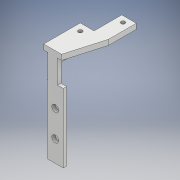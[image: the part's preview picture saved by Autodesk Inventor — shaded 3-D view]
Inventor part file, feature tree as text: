
AUTODESK INVENTOR PART (.ipt)
format: ipt  version: 2018.3 (Build 223284000, 284)  size: 1,041,408 bytes
history: native  units: mm
features: extrude x95, sketch x95, other x2
ambient origin geometry x8: Origin, YZ Plane, XZ Plane, XY Plane, X Axis, Y Axis, Z Axis, Center Point
bodies: Body1 (feature_tree), Body2 (feature_tree)
feature tree (192):
  other  "Sólido1"
  extrude  "Extrusión1"  Depth=10.0mm TaperAngle=0.0deg
  extrude  "Extrusión2"  Depth=33.0mm TaperAngle=0.0deg
  extrude  "Extrusión3"  Depth=29.0mm TaperAngle=0.0deg
  extrude  "Extrusión4"  Depth=21.0mm
  extrude  "Extrusión5"  Depth=4.0mm TaperAngle=0.0deg
  extrude  "Extrusión6"  Depth=37.0mm TaperAngle=0.0deg
  extrude  "Extrusión7"  Depth=94.0mm TaperAngle=0.0deg
  extrude  "Extrusión8"  Depth=15.0mm
  extrude  "Extrusión9"  Depth=64.0mm TaperAngle=0.0deg
  extrude  "Extrusión10"  Depth=10.0mm
  extrude  "Extrusión11"  Depth=64.0mm TaperAngle=0.0deg
  extrude  "Extrusión13"  Depth=10.0mm
  extrude  "Extrusión14"  Depth=10.0mm
  extrude  "Extrusión15"  Depth=19.0mm TaperAngle=0.0deg
  extrude  "Extrusión17"  Depth=19.0mm TaperAngle=0.0deg
  extrude  "Extrusión18"  Depth=15.0mm TaperAngle=0.0deg
  extrude  "Extrusión19"  Depth=3.0mm
  extrude  "Extrusión20"  Depth=6.0mm TaperAngle=0.0deg
  extrude  "Extrusión21"  Depth=10.0mm TaperAngle=0.0deg
  extrude  "Extrusión22"  Depth=10.0mm TaperAngle=0.0deg
  extrude  "Extrusión23"  Depth=10.0mm TaperAngle=0.0deg
  extrude  "Extrusión27"  Depth=15.0mm
  extrude  "Extrusión28"  Depth=5.0mm
  extrude  "Extrusión29"  Depth=4.0mm TaperAngle=0.0deg
  extrude  "Extrusión30"  Depth=24.5mm TaperAngle=0.0deg
  extrude  "Extrusión31"  Depth=24.5mm TaperAngle=0.0deg
  extrude  "Extrusión32"  Depth=4.3mm
  extrude  "Extrusión33"  Depth=3.7mm
  sketch  "Boceto34"  dims[d152=3.7mm d153=3.7mm]
  extrude  "Extrusión35"  Depth=3.7mm
  extrude  "Extrusión36"  Depth=25.5mm TaperAngle=0.0deg
  extrude  "Extrusión38"  Depth=5.2mm
  extrude  "Extrusión39"  Depth=5.2mm
  extrude  "Extrusión40"  Depth=45.25mm TaperAngle=0.0deg
  extrude  "Extrusión41"  Depth=71.0mm TaperAngle=0.0deg
  extrude  "Extrusión42"  Depth=1.7mm TaperAngle=0.0deg
  extrude  "Extrusión43"  Depth=33.0mm
  extrude  "Extrusión44"  Depth=2.4mm TaperAngle=0.0deg
  extrude  "Extrusión45"  Depth=85.9mm TaperAngle=0.0deg
  extrude  "Extrusión46"  Depth=2.973mm
  extrude  "Extrusión47"  Depth=3.7mm
  extrude  "Extrusión48"  Depth=3.7mm
  extrude  "Extrusión49"  Depth=5.0mm TaperAngle=0.0deg
  extrude  "Extrusión50"  Depth=0.534mm
  extrude  "Extrusión53"  Depth=2.384mm TaperAngle=0.0deg
  extrude  "Extrusión54"  Depth=5.884mm TaperAngle=0.0deg
  extrude  "Extrusión55"  Depth=14.25mm TaperAngle=0.0deg
  extrude  "Extrusión56"  Depth=11.0mm TaperAngle=0.0deg
  extrude  "Extrusión57"  Depth=3.1mm
  sketch  "Boceto57"  dims[d235=11.0mm d236=0.0mm d237=11.0mm]
  extrude  "Extrusión58"  Depth=11.0mm
  extrude  "Extrusión59"  Depth=11.0mm TaperAngle=0.0deg
  extrude  "Extrusión60"  Depth=13.0mm TaperAngle=0.0deg
  extrude  "Extrusión61"  Depth=14.0mm TaperAngle=0.0deg
  extrude  "Extrusión62"  Depth=4.3mm
  extrude  "Extrusión63"  Depth=5.0mm TaperAngle=0.0deg
  extrude  "Extrusión64"  Depth=21.5mm TaperAngle=0.0deg
  extrude  "Extrusión65"  Depth=8.0mm TaperAngle=0.0deg
  extrude  "Extrusión66"  Depth=8.0mm TaperAngle=0.0deg
  extrude  "Extrusión67"  Depth=4.0mm TaperAngle=0.0deg
  extrude  "Extrusión68"  Depth=8.0mm TaperAngle=0.0deg
  extrude  "Extrusión69"  Depth=4.0mm TaperAngle=0.0deg
  extrude  "Extrusión74"  Depth=4.3mm TaperAngle=0.0deg
  extrude  "Extrusión75"  Depth=15.0mm TaperAngle=0.0deg
  extrude  "Extrusión76"  Depth=15.0mm TaperAngle=0.0deg
  extrude  "Extrusión77"  Depth=15.0mm TaperAngle=0.0deg
  extrude  "Extrusión78"  Depth=79.25mm TaperAngle=0.0deg
  extrude  "Extrusión79"  Depth=5.0mm TaperAngle=0.0deg
  extrude  "Extrusión80"  Depth=4.0mm TaperAngle=0.0deg
  extrude  "Extrusión81"  Depth=3.0mm
  extrude  "Extrusión82"  Depth=2.53mm TaperAngle=0.0deg
  extrude  "Extrusión83"  Depth=4.0mm TaperAngle=0.0deg
  extrude  "Extrusión84"  Depth=2.6mm TaperAngle=0.0deg
  extrude  "Extrusión85"  Depth=5.2mm TaperAngle=0.0deg
  extrude  "Extrusión86"  Depth=46.25mm TaperAngle=0.0deg
  extrude  "Extrusión87"  [1 undecoded]
  extrude  "Extrusión88"  [1 undecoded]
  extrude  "Extrusión89"  [1 undecoded]
  extrude  "Extrusión90"  [1 undecoded]
  extrude  "Extrusión91"  [1 undecoded]
  extrude  "Extrusión92"  [1 undecoded]
  extrude  "Extrusión93"  [1 undecoded]
  extrude  "Extrusión94"  [1 undecoded]
  extrude  "Extrusión95"  [1 undecoded]
  extrude  "Extrusión96"  [1 undecoded]
  extrude  "Extrusión97"  [1 undecoded]
  extrude  "Extrusión98"  [1 undecoded]
  extrude  "Extrusión99"  [1 undecoded]
  extrude  "Extrusión100"  [1 undecoded]
  extrude  "Extrusión101"  [1 undecoded]
  extrude  "Extrusión102"  [1 undecoded]
  extrude  "Extrusión103"  [1 undecoded]
  extrude  "Extrusión104"  [1 undecoded]
  extrude  "Extrusión105"  [1 undecoded]
  extrude  "Extrusión106"  [1 undecoded]
  extrude  "Extrusión107"  [1 undecoded]
  extrude  "Extrusión108"  [1 undecoded]
  sketch  "Boceto1"  dims[d0=18.0mm d1=0.0mm d2=10.0mm d3=0.0mm]
  sketch  "Boceto2"  dims[d6=3.0mm d7=33.0mm d8=0.0mm]
  sketch  "Boceto4"  dims[d9=35.0mm d10=29.0mm d11=0.0mm]
  sketch  "Boceto5"  dims[d12=2.0mm d13=21.0mm]
  sketch  "Boceto6"  dims[d14=20.0mm d15=4.0mm d16=0.0mm]
  sketch  "Boceto7"  dims[d17=8.0mm d18=0.0mm d19=37.0mm d20=0.0mm]
  sketch  "Boceto8"  dims[d21=2.0mm d22=94.0mm d23=0.0mm]
  sketch  "Boceto9"  dims[d30=5.0mm d31=15.0mm]
  sketch  "Boceto12"  dims[d32=15.0mm d33=64.0mm d34=0.0mm]
  sketch  "Boceto13"  dims[d35=64.0mm d36=0.0mm d38=10.0mm]
  sketch  "Boceto15"  dims[d40=15.0mm d41=64.0mm d42=0.0mm]
  sketch  "Boceto17"  dims[d48=46.25mm d49=10.0mm]
  sketch  "Boceto18"  dims[d50=23.0mm d51=0.0mm d52=10.0mm]
  sketch  "Boceto19"  dims[d53=19.0mm d54=0.0mm d58=19.0mm d59=0.0mm]
  sketch  "Boceto20"  dims[d68=19.0mm d69=0.0mm d70=19.0mm d71=0.0mm]
  sketch  "Boceto21"  dims[d73=19.0mm d74=0.0mm d76=15.0mm d77=0.0mm]
  sketch  "Boceto22"  dims[d78=4.0mm d79=0.0mm d80=3.0mm]
  sketch  "Boceto23"  dims[d81=6.0mm d82=0.0mm d87=6.0mm d88=0.0mm]
  sketch  "Boceto24"  dims[d89=4.0mm d96=10.0mm d97=0.0mm]
  sketch  "Boceto25"  dims[d101=10.0mm d102=0.0mm d104=10.0mm d105=0.0mm]
  sketch  "Boceto26"  dims[d106=2.0mm d107=10.0mm d108=0.0mm]
  sketch  "Boceto27"  dims[d110=11.0mm d111=15.0mm]
  sketch  "Boceto28"  dims[d112=10.0mm d113=0.0mm d114=5.0mm]
  sketch  "Boceto29"  dims[d115=23.0mm d116=0.0mm d117=4.0mm d118=0.0mm]
  sketch  "Boceto30"  dims[d124=24.5mm d125=0.0mm d132=24.5mm d133=0.0mm]
  sketch  "Boceto31"  dims[d141=24.5mm d142=0.0mm d145=24.5mm d146=0.0mm]
  sketch  "Boceto32"  dims[d147=10.0mm d148=0.0mm d149=4.3mm]
  sketch  "Boceto33"  dims[d150=4.3mm d151=3.7mm]
  sketch  "Boceto35"  dims[d154=3.7mm d155=25.5mm d156=0.0mm]
  sketch  "Boceto37"  dims[d157=5.2mm d158=5.2mm]
  sketch  "Boceto38"  dims[d159=25.5mm d160=0.0mm d161=5.2mm]
  sketch  "Boceto39"  dims[d162=5.2mm d163=45.25mm d164=0.0mm]
  sketch  "Boceto40"  dims[d165=2.6mm d166=71.0mm d167=0.0mm]
  sketch  "Boceto41"  dims[d168=10.005mm d169=1.7mm d170=0.0mm]
  sketch  "Boceto42"  dims[d171=33.0mm d172=33.0mm]
  sketch  "Boceto43"  dims[d173=38.28mm d174=4.0mm d175=0.0mm d176=0.0mm d178=2.4mm d179=0.0mm]
  sketch  "Boceto44"  dims[d180=6.15mm d181=0.0mm d184=85.9mm d185=0.0mm]
  sketch  "Boceto45"  dims[d186=2.973mm d187=2.973mm]
  sketch  "Boceto46"  dims[d188=5.0mm d189=0.0mm d205=3.7mm]
  sketch  "Boceto47"  dims[d209=3.7mm d210=3.7mm]
  sketch  "Boceto48"  dims[d211=3.7mm d212=5.0mm d213=0.0mm]
  sketch  "Boceto49"  dims[d214=5.0mm d215=0.0mm d216=0.534mm]
  sketch  "Boceto50"  dims[d217=5.0mm d218=0.0mm d219=2.384mm d220=0.0mm]
  sketch  "Boceto53"  dims[d221=17.6mm d222=5.884mm d223=0.0mm]
  sketch  "Boceto54"  dims[d224=3.25mm d225=14.25mm d226=0.0mm]
  sketch  "Boceto55"  dims[d227=11.0mm d228=0.0mm d229=11.0mm d230=0.0mm]
  sketch  "Boceto56"  dims[d233=3.1mm d234=3.1mm]
  sketch  "Boceto58"  dims[d238=11.0mm d239=11.0mm d240=0.0mm]
  sketch  "Boceto59"  dims[d241=11.0mm d242=0.0mm d243=13.0mm d244=0.0mm]
  sketch  "Boceto60"  dims[d245=23.0mm d246=0.0mm d247=14.0mm d248=0.0mm]
  sketch  "Boceto61"  dims[d249=15.0mm d250=0.0mm d251=4.3mm]
  sketch  "Boceto62"  dims[d252=8.0mm d253=0.0mm d254=5.0mm d255=0.0mm]
  sketch  "Boceto63"  dims[d268=1.0mm d269=21.5mm d270=0.0mm]
  sketch  "Boceto64"  dims[d271=0.389mm d272=8.0mm d273=0.0mm]
  sketch  "Boceto65"  dims[d276=8.0mm d277=0.0mm d279=8.0mm d280=0.0mm]
  sketch  "Boceto66"  dims[d282=8.0mm d283=0.0mm d285=4.0mm d286=0.0mm]
  sketch  "Boceto67"  dims[d288=4.0mm d289=0.0mm d291=8.0mm d292=0.0mm]
  sketch  "Boceto70"  dims[d293=0.135mm d294=4.0mm d295=0.0mm]
  sketch  "Boceto75"  dims[d296=4.3mm d297=0.0mm d299=4.3mm d300=0.0mm]
  sketch  "Boceto76"  dims[d303=15.0mm d304=0.0mm d306=15.0mm d307=0.0mm]
  sketch  "Boceto77"  dims[d309=15.0mm d310=0.0mm d311=15.0mm d312=0.0mm]
  sketch  "Boceto78"  dims[d314=15.0mm d315=0.0mm d316=15.0mm d317=0.0mm]
  sketch  "Boceto79"  dims[d318=1.17mm d319=0.0mm d320=79.25mm d321=0.0mm]
  sketch  "Boceto80"  dims[d334=5.0mm d335=0.0mm d336=5.0mm d337=0.0mm]
  sketch  "Boceto81"  dims[d338=0.03mm d339=0.0mm d340=4.0mm d341=0.0mm]
  sketch  "Boceto82"  dims[d342=4.0mm d343=0.0mm d344=3.0mm]
  sketch  "Boceto83"  dims[d345=4.0mm d346=0.0mm d347=2.53mm d348=0.0mm]
  sketch  "Boceto84"  dims[d349=4.0mm d350=0.0mm d352=4.0mm d353=0.0mm]
  sketch  "Boceto86"  dims[d354=5.0mm d355=0.0mm d356=2.6mm d357=0.0mm]
  sketch  "Boceto87"  dims[d361=5.2mm d362=0.0mm d365=5.2mm d366=0.0mm]
  sketch  "Boceto88"  dims[d367=46.25mm d368=0.0mm d369=46.25mm d370=0.0mm]
  sketch  "Boceto89"  dims[d371=2.6mm d372=0.0mm]
  sketch  "Boceto90"
  sketch  "Boceto91"
  sketch  "Boceto92"
  sketch  "Boceto93"
  sketch  "Boceto94"
  sketch  "Boceto95"
  sketch  "Boceto96"
  sketch  "Boceto97"
  sketch  "Boceto99"
  sketch  "Boceto100"
  sketch  "Boceto101"
  sketch  "Boceto102"
  sketch  "Boceto103"
  sketch  "Boceto104"
  sketch  "Boceto105"
  sketch  "Boceto106"
  sketch  "Boceto107"
  sketch  "Boceto108"
  sketch  "Boceto111"
  sketch  "Boceto112"
  sketch  "Boceto113"
  other  "Saliente-Extruir7"
note: 22 required parameter values undecoded (feature->parameter linkage not recoverable at this tier; creation-order binding heuristic only, values carry confidence <= 0.55)
